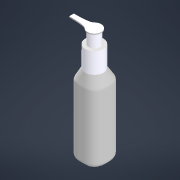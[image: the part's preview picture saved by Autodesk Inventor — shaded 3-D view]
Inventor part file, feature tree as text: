
AUTODESK INVENTOR PART (.ipt)
format: ipt  version: 2022 (Build 260153000, 153)  size: 321,024 bytes
history: native  units: in
note: dims shown in document units (in); Inventor stores cm internally (conversion verified against a paired STEP export)
features: extrude x4, sketch x4, other x4, projected_geometry x2, plane x1, loft x1, fillet x1, reference x1
ambient origin geometry x8: Origin, YZ Plane, XZ Plane, XY Plane, X Axis, Y Axis, Z Axis, Center Point
bodies: Solid1 (feature_tree)
feature tree (18):
  extrude  "Extrusion1"  Depth=1.5in
  plane  "Work Plane1"
  loft  "Loft1"
  extrude  "Extrusion2"  Depth=1.0in
  extrude  "Extrusion3"  TaperAngle=0.0deg  [1 undecoded]
  extrude  "Extrusion5"  Depth=1.125in TaperAngle=0.0deg
  fillet  "Fillet1"  Radius=0.625in
  sketch  "Sketch2"  dims[d0=1.5in d1=1.5in]
  projected_geometry  "Projected Loop1"
  other  "Edges1"
  sketch  "Sketch3"  dims[d2=0.25in d3=3.5in d4=0.0in]
  projected_geometry  "Projected Loop2"
  sketch  "Sketch4"  dims[d5=0.5in d6=1.0in]
  sketch  "Sketch5"  dims[d7=0.0in d8=90.0deg d9=0.0in d10=90.0deg d11=1.125in d12=0.0in d13=0.625in d14=0.75in d15=0.0in d16=0.75in d19=1.25in d20=0.125in d21=0.0625in d22=0.0in d23=0.25in d24=0.875in d25=0.875in]
  reference  "Reference1"
  parser-record x1  (decoder bookkeeping rows leaked as tree rows — omitted from the tree; the rows remain in map.json)
  other  "Prototype Assembly.iam"
  other  "Prototype Base:1"
note: 1 required parameter value undecoded (feature->parameter linkage not recoverable at this tier; creation-order binding heuristic only, values carry confidence <= 0.55)
note: 1 file-system path scrubbed to <path> (originals preserved in map.json)
